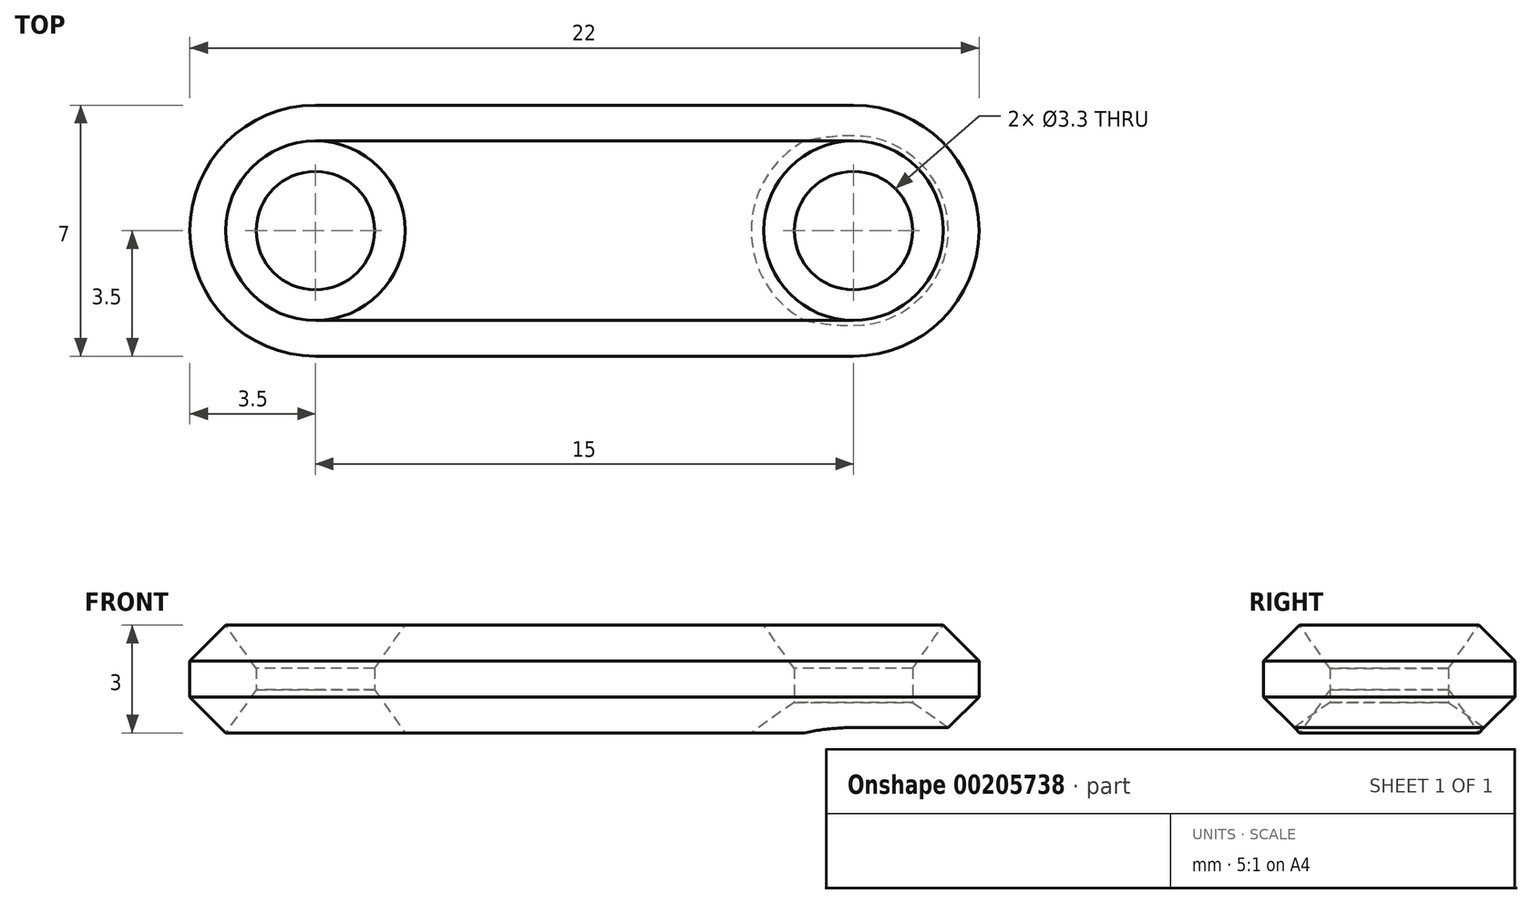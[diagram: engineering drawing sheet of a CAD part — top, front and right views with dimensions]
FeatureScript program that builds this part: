
annotation { "Feature Type Name" : "Feature", "Feature Type Description" : "" }
export const myFeature = defineFeature(function(context is Context, id is Id, definition is map)
    precondition{}
    {
        {
            var Q0;
            Q0=qCreatedBy(makeId("Top.planeOp"),FACE);
            var sketch = newSketch(context, id + "F0", { "sketchPlane" : qUnion([Q0])});
            skLineSegment(sketch, "E0", {"start": v(0, 0) * mm, "end": v(-15, 0) * mm, "construction": true});
            skCircle(sketch, "E1", {"center": v(-15, 0) * mm, "radius": 3.5 * mm});
            skCircle(sketch, "E2", {"center": v(0, 0) * mm, "radius": 3.5 * mm});
            skCircle(sketch, "E3", {"center": v(-15, 0) * mm, "radius": 1.65 * mm});
            skLineSegment(sketch, "E4", {"start": v(-15, 3.5) * mm, "end": v(0, 3.5) * mm});
            skLineSegment(sketch, "E5", {"start": v(0, -3.5) * mm, "end": v(-15, -3.5) * mm});
            skCircle(sketch, "E6", {"center": v(0, 0) * mm, "radius": 1.65 * mm});
            skSolve(sketch);
        }
        {
            var Q0;
            Q0=makeQuery(id+"F0.imprint","IMPRINT",FACE,{"disambiguationData":[TD([[makeQuery(id+"F0.imprint","IMPRINT",EDGE,{"derivedFrom":sQuery(id+"F0.wireOp",EDGE,"E3")}),-1.0]])]});
            var Q1;
            {var subQ0=sQuery(id+"F0.wireOp",EDGE,"E4");Q1=makeQuery(id+"F0.imprint","IMPRINT",FACE,{"disambiguationData":[TD([[makeQuery(id+"F0.imprint","IMPRINT",EDGE,{"derivedFrom":subQ0}),-1.0]])]});}
            var Q2;
            Q2=makeQuery(id+"F0.imprint","IMPRINT",FACE,{"disambiguationData":[TD([[makeQuery(id+"F0.imprint","IMPRINT",EDGE,{"derivedFrom":sQuery(id+"F0.wireOp",EDGE,"E6")}),-1.0]])]});
            extrude(context, id + "F1", {"entities" : qUnion([Q0, Q1, Q2]), "depth" : 3 * mm});
        }
        {
            var Q0;
            Q0=makeQuery(id+"F1.opExtrude","CAP_EDGE",EDGE,{"disambiguationData":[OSD([sQuery(id+"F0.wireOp",EDGE,"E5")])],"isStart":false});
            var Q1;
            Q1=makeQuery(id+"F1.opExtrude","CAP_EDGE",EDGE,{"disambiguationData":[OSD([sQuery(id+"F0.wireOp",EDGE,"E1")])],"isStart":false});
            var Q2;
            Q2=makeQuery(id+"F1.opExtrude","CAP_EDGE",EDGE,{"disambiguationData":[OSD([sQuery(id+"F0.wireOp",EDGE,"E2")])],"isStart":false});
            var Q3;
            Q3=makeQuery(id+"F1.opExtrude","CAP_EDGE",EDGE,{"disambiguationData":[OSD([sQuery(id+"F0.wireOp",EDGE,"E4")])],"isStart":false});
            var Q4;
            Q4=makeQuery(id+"F1.opExtrude","CAP_EDGE",EDGE,{"disambiguationData":[OSD([sQuery(id+"F0.wireOp",EDGE,"E5")])],"isStart":true});
            chamfer(context, id + "F2", {"entities" : qUnion([Q0, Q1, Q2, Q3, Q4]), "width" : 1 * mm, "tangentPropagation" : true});
        }
        {
            var Q0;
            Q0=makeQuery(id+"F1.opExtrude","CAP_EDGE",EDGE,{"disambiguationData":[OSD([sQuery(id+"F0.wireOp",EDGE,"E3")])],"isStart":false});
            var Q1;
            Q1=makeQuery(id+"F1.opExtrude","CAP_EDGE",EDGE,{"disambiguationData":[OSD([sQuery(id+"F0.wireOp",EDGE,"E6")])],"isStart":false});
            var Q2;
            Q2=makeQuery(id+"F1.opExtrude","CAP_EDGE",EDGE,{"disambiguationData":[OSD([sQuery(id+"F0.wireOp",EDGE,"E6")])],"isStart":true});
            var Q3;
            Q3=makeQuery(id+"F1.opExtrude","CAP_EDGE",EDGE,{"disambiguationData":[OSD([sQuery(id+"F0.wireOp",EDGE,"E3")])],"isStart":true});
            chamfer(context, id + "F3", {"entities" : qUnion([Q0, Q1, Q2, Q3]), "chamferType" : ChamferType.TWO_OFFSETS, "width1" : 1.2 * mm, "oppositeDirection" : false, "width2" : 0.85 * mm, "tangentPropagation" : true});
        }
    });
